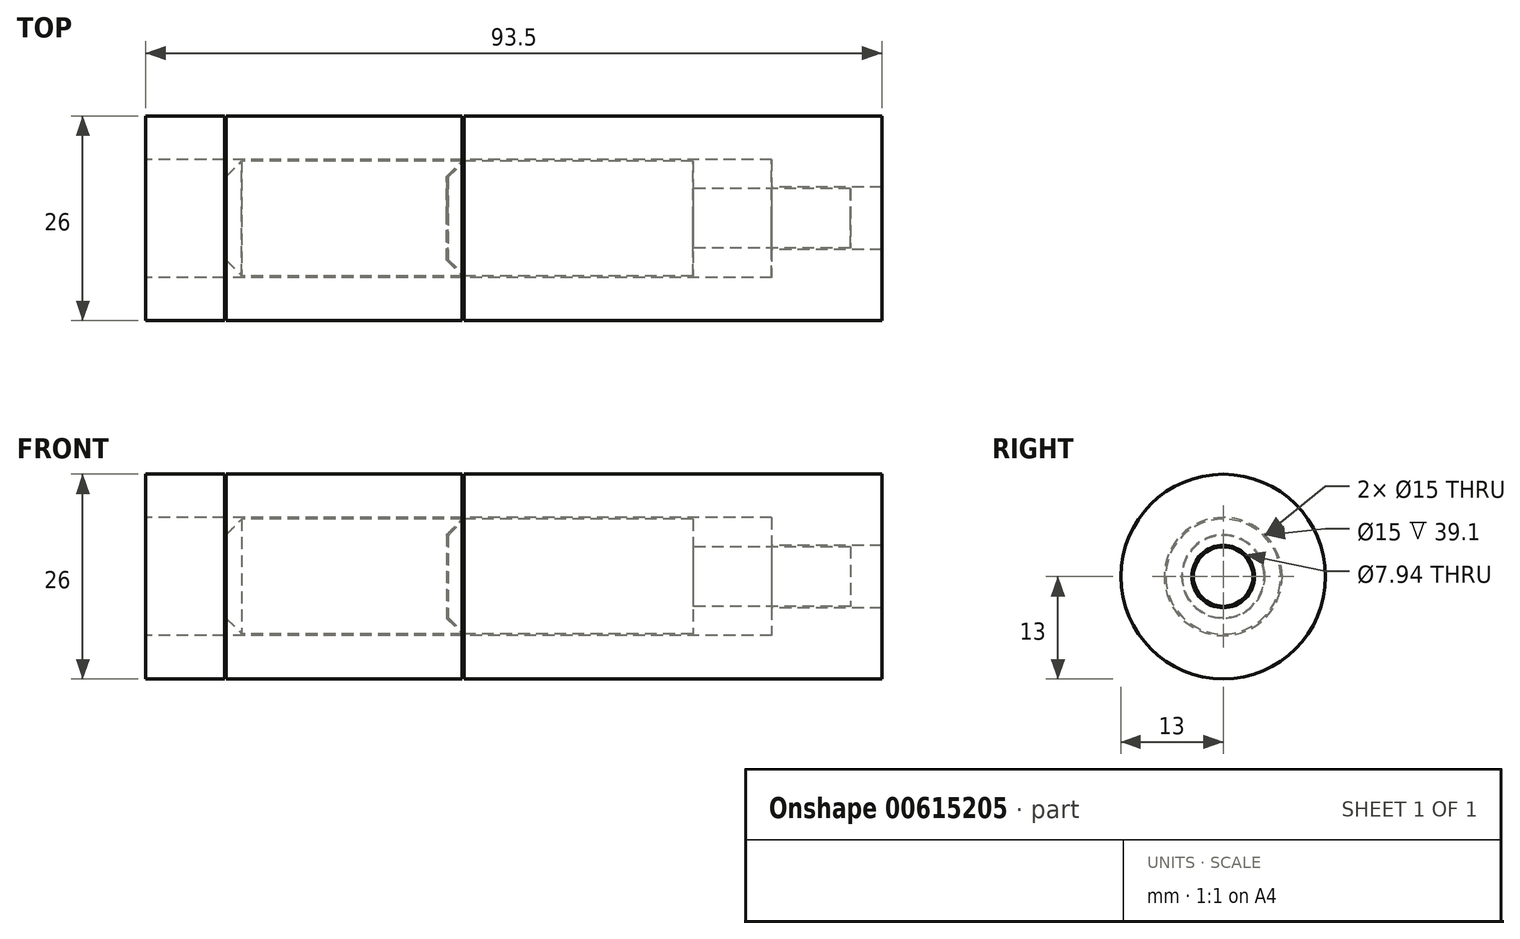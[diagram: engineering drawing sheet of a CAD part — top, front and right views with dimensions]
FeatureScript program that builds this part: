
annotation { "Feature Type Name" : "Feature", "Feature Type Description" : "" }
export const myFeature = defineFeature(function(context is Context, id is Id, definition is map)
    precondition{}
    {
        {
            var Q0;
            Q0=qCreatedBy(makeId("Top.planeOp"),FACE);
            var sketch = newSketch(context, id + "F0", { "sketchPlane" : qUnion([Q0])});
            skLineSegment(sketch, "E0.bottom", {"start": v(-93.5, 13) * mm, "end": v(-83.5, 13) * mm});
            skLineSegment(sketch, "E0.top", {"start": v(-93.5, 0) * mm, "end": v(-83.5, 0) * mm});
            skLineSegment(sketch, "E0.left", {"start": v(-93.5, 13) * mm, "end": v(-93.5, 0) * mm});
            skLineSegment(sketch, "E0.right", {"start": v(-83.5, 13) * mm, "end": v(-83.5, 0) * mm});
            skLineSegment(sketch, "E1.bottom", {"start": v(-53.1, 13) * mm, "end": v(0, 13) * mm});
            skLineSegment(sketch, "E1.top", {"start": v(-53.1, 0) * mm, "end": v(0, 0) * mm});
            skLineSegment(sketch, "E1.left", {"start": v(-53.1, 13) * mm, "end": v(-53.1, 0) * mm});
            skLineSegment(sketch, "E1.right", {"start": v(0, 13) * mm, "end": v(0, 0) * mm});
            skLineSegment(sketch, "E2", {"start": v(-93.5, 7.5) * mm, "end": v(-83.5, 7.5) * mm});
            skLineSegment(sketch, "E3", {"start": v(-53.1, 7.5) * mm, "end": v(0, 7.5) * mm});
            skLineSegment(sketch, "E4.bottom", {"start": v(-83.3, 13) * mm, "end": v(-53.3, 13) * mm});
            skLineSegment(sketch, "E4.top", {"start": v(-83.3, 0) * mm, "end": v(-53.3, 0) * mm});
            skLineSegment(sketch, "E4.left", {"start": v(-83.3, 13) * mm, "end": v(-83.3, 0) * mm});
            skLineSegment(sketch, "E4.right", {"start": v(-53.3, 13) * mm, "end": v(-53.3, 0) * mm});
            skLineSegment(sketch, "E5", {"start": v(-83.3, 7.5) * mm, "end": v(-53.3, 7.5) * mm});
            skLineSegment(sketch, "E6", {"start": v(-83.3, 5.3) * mm, "end": v(-81.3, 7.3) * mm});
            skLineSegment(sketch, "E7", {"start": v(-81.3, 7.3) * mm, "end": v(-53.3, 7.3) * mm});
            skLineSegment(sketch, "E8", {"start": v(-53.3, 7.3) * mm, "end": v(-55.3, 5.3) * mm});
            skLineSegment(sketch, "E9", {"start": v(-55.3, 5.3) * mm, "end": v(-55.3, 0) * mm});
            skLineSegment(sketch, "E10", {"start": v(-55.1, 0) * mm, "end": v(-55.1, 5.22) * mm});
            skLineSegment(sketch, "E11", {"start": v(-55.1, 5.22) * mm, "end": v(-53.02, 7.3) * mm});
            skLineSegment(sketch, "E12", {"start": v(-53.02, 7.3) * mm, "end": v(-24, 7.3) * mm});
            skLineSegment(sketch, "E13", {"start": v(-53.3, 0) * mm, "end": v(-53.1, 0) * mm});
            skLineSegment(sketch, "E14", {"start": v(-24, 7.3) * mm, "end": v(-24, 3.77) * mm});
            skLineSegment(sketch, "E15", {"start": v(-24, 3.77) * mm, "end": v(-4, 3.77) * mm});
            skLineSegment(sketch, "E16", {"start": v(-4, 3.77) * mm, "end": v(-4, 0) * mm});
            skLineSegment(sketch, "E17", {"start": v(-14, 7.5) * mm, "end": v(-14, 3.97) * mm});
            skLineSegment(sketch, "E18", {"start": v(-14, 3.97) * mm, "end": v(0, 3.97) * mm});
            skSolve(sketch);
        }
        {
            var Q0;
            {var subQ0=sQuery(id+"F0.wireOp",EDGE,"E0.bottom");Q0=makeQuery(id+"F0.imprint","IMPRINT",FACE,{"disambiguationData":[TD([[makeQuery(id+"F0.imprint","IMPRINT",EDGE,{"derivedFrom":subQ0}),-1.0]])]});}
            var Q1;
            {var subQ0=sQuery(id+"F0.wireOp",EDGE,"E4.bottom");Q1=makeQuery(id+"F0.imprint","IMPRINT",FACE,{"disambiguationData":[TD([[makeQuery(id+"F0.imprint","IMPRINT",EDGE,{"derivedFrom":subQ0}),-1.0]])]});}
            var Q2;
            {var subQ0=sQuery(id+"F0.wireOp",EDGE,"E1.bottom");Q2=makeQuery(id+"F0.imprint","IMPRINT",FACE,{"disambiguationData":[TD([[makeQuery(id+"F0.imprint","IMPRINT",EDGE,{"derivedFrom":subQ0}),-1.0]])]});}
            var Q3;
            {var subQ0=sQuery(id+"F0.wireOp",EDGE,"E6");Q3=makeQuery(id+"F0.imprint","IMPRINT",FACE,{"disambiguationData":[TD([[makeQuery(id+"F0.imprint","IMPRINT",EDGE,{"derivedFrom":subQ0}),-1.0]])]});}
            var Q4;
            {var subQ3=sQuery(id+"F0.wireOp",EDGE,"E10");Q4=makeQuery(id+"F0.imprint","IMPRINT",FACE,{"disambiguationData":[TD([[makeQuery(id+"F0.imprint","IMPRINT",EDGE,{"derivedFrom":subQ3}),-1.0]])]});}
            var Q5;
            {var subQ0=sQuery(id+"F0.wireOp",EDGE,"E13");Q5=makeQuery(id+"F0.imprint","IMPRINT",FACE,{"disambiguationData":[TD([[makeQuery(id+"F0.imprint","IMPRINT",EDGE,{"derivedFrom":subQ0}),1.0]])]});}
            var Q6;
            {var subQ0=sQuery(id+"F0.wireOp",EDGE,"E12");Q6=makeQuery(id+"F0.imprint","IMPRINT",FACE,{"disambiguationData":[TD([[makeQuery(id+"F0.imprint","IMPRINT",EDGE,{"derivedFrom":subQ0}),-1.0]])]});}
            var Q7;
            {var subQ4=sQuery(id+"F0.wireOp",EDGE,"E17");Q7=makeQuery(id+"F0.imprint","IMPRINT",FACE,{"disambiguationData":[TD([[makeQuery(id+"F0.imprint","IMPRINT",EDGE,{"derivedFrom":subQ4}),1.0]])]});}
            var Q8;
            Q8=sQuery(id+"F0.wireOp",EDGE,"E1.top");
            revolve(context, id + "F1", {"entities" : qUnion([Q0, Q1, Q2, Q3, Q4, Q5, Q6, Q7]), "axis" : qUnion([Q8]), "revolveType" : RevolveType.FULL});
        }
    });
